# Revit family: xxxFloor_Drain-Can_Washing-J.R_Smith-Sani_Ceptor-3370_Series
name_source: partatom
category: Plumbing Fixtures
units: mm (PartAtom-declared; Revit-internal decimal feet)

## family parameters
Always vertical = No
Cut with Voids When Loaded = No
OmniClass Number = 23.70.50.21.24
OmniClass Title = Waste Water Drains
Part Type = Normal
Room Calculation Point = No
Round Connector Dimension = Use Diameter
Shared = Yes
Work Plane-Based = Yes

## types (6) — shared parameters
Assembly Code = D2030300
C - flashing clamp = No
CW Connection = No
Default Elevation = 0"
Description = Sani-Ceptor® Can Washing Sanitary Floor Drains
Finish = Metal-Jay R. Smith-Cast Iron
Finish- Rim and Grate = Metal-Jay R. Smith-Nickel Bronze
HW Connection = No
Installation Type = Floor Mounted
L - Speedi-Set Service Weight = No
LXH - Speedi-Set Extra Heavy = No
Length = 12 1/2"
Manufacturer = Jay R. Smith
Material = Metal-Jay R. Smith-Cast Iron
NPT Connection Diameter = 1/2"
PB- Polished Bronze Rim and Grate = No
Product Documentation Link = https://www.jrsmith.com
Product Page URL = https://www.jrsmith.com
Radius-C = 2"
Tempered Water Connection = Yes
URL = https://www.jrsmith.com
Vent Connection = No
Waste Connection = Yes
Width = 12 1/2"
zero-valued in all types: CWFU, HWFU, WFU

## per-type parameters (varying)
| type | Connection Type | Pipe Connection Size |
| 3370C02 | 2" Caulk Outlet Connection | 2" |
| 3370C04 | 4" Caulk Outlet Connection | 4" |
| 3370Y02 | 2" No-Hub Outlet Connection | 2" |
| 3370Y03 | 3" No-Hub Outlet Connection | 3" |
| 3370Y04 | 4" No-Hub Outlet Connection | 4" |
| 3370C03 | 3" Caulk Outlet Connection | 3" |

note: column(s) folded — value = type name in every type: Model

## geometry (parser evidence)
native form markers: Sweep x1
no freeform markers — native parametric forms only
